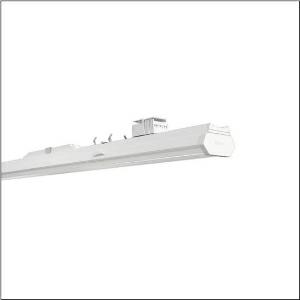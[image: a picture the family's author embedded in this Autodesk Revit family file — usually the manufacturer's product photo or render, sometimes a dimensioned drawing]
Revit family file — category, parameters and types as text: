
# Revit family: licross_r__11_protected_ho_51tp13mn4gxs_4b4b
name_source: partatom
category: Lighting Fixtures
units: mm (PartAtom-declared; Revit-internal decimal feet)

## family parameters
Cut with Voids When Loaded = No
Host = Face
Light Source = No
Part Type = Normal
Room Calculation Point = No
Round Connector Dimension = Use Diameter
Shared = No

## types (1)
- --- (1 x LED, 16110 lm, 87.4 W, 4000K)
    Apparent Load = 87 VA
    CIE Flux Codes = 89 96 99 100 99
    Color Rendering = 80
    Color Temperature = 4000K
    Default Elevation = 1800 mm
    Description = Licross® 11 Protected HO, luminaire insert, of sheet steel, galvanised, coil coated, white, length: 1.500mm, width: 90mm, height: 101mm, LED rated luminous flux: 16.110lm, light colour: 840, control gear: ON/OFF Multilumen, control gear: ECG Multilumen, with plug, 3-pole, with phase selection, mains connection: 220..240V, AC, 50/60Hz, halogen-free wiring, primary light control with lens, of plastic, primary optical cover: cover, of PMMA, light emission: direct with ceiling illumination distribution, primary light characteristic: symmetric, protection rating (complete): IP64, insulation class (complete): insulation class I (protective earthing), certification: CE, ENEC, VDE, UKCA, protection symbol: D if used in an environment with conductive dust loads with corresponding accessories, impact resistance: IK06, permissible ambient temperature for indoor applications: -35..+35°C, corresponds to IFS (International Featured Standards) requirements for safety and quality in the food industry, reducing of maximum allowable ambient temperature of 5°C with ceiling mounting, LABS conformity tested according to VDMA 24364:2018-05, packaging unit: 1 piece
    Height = 92 mm
    Lamp = 1 x LED
    Lamp Light Flux = 16110 lm
    Lamp Power = 87.4 W
    Lamp count = 1
    Length = 1500 mm
    Luminous efficacy = 184 lm/W
    Manufacturer = Siteco
    ModVariant = No
    Model = 51TP13MN4GXS
    Mounting Place = Ceiling
    Mounting Type = Pendant
    Number of Poles = 1
    OnlyDefault = Yes
    Power Factor = 1
    Product Name = Licross® 11 Protected HO
    Product group = luminaire insert
    ProductGroupID = 902
    Protection Class = Protection class I
    Protection Degree = IP 64
    RLX_Detail_Level = 1
    RlxData = <blob elided: 22005 chars, md5=df9f8d19>
    Socket = socket
    Standby Power = 0 W
    System Light Flux = 16110 lm
    System Power = 87 W
    Type Comments = factory setting: luminous flux: 100 % | (A | C | E) | 203 mA
    Type Image = l_1256148.jpg
    URL = http://relux.com
    VarID = @adj_003655
    Voltage = 0 V
    Weight = 0.00 kg
    Width = 88 mm

## geometry (parser evidence)
native form markers: Blend x4, Sweep x13
no freeform markers — native parametric forms only
